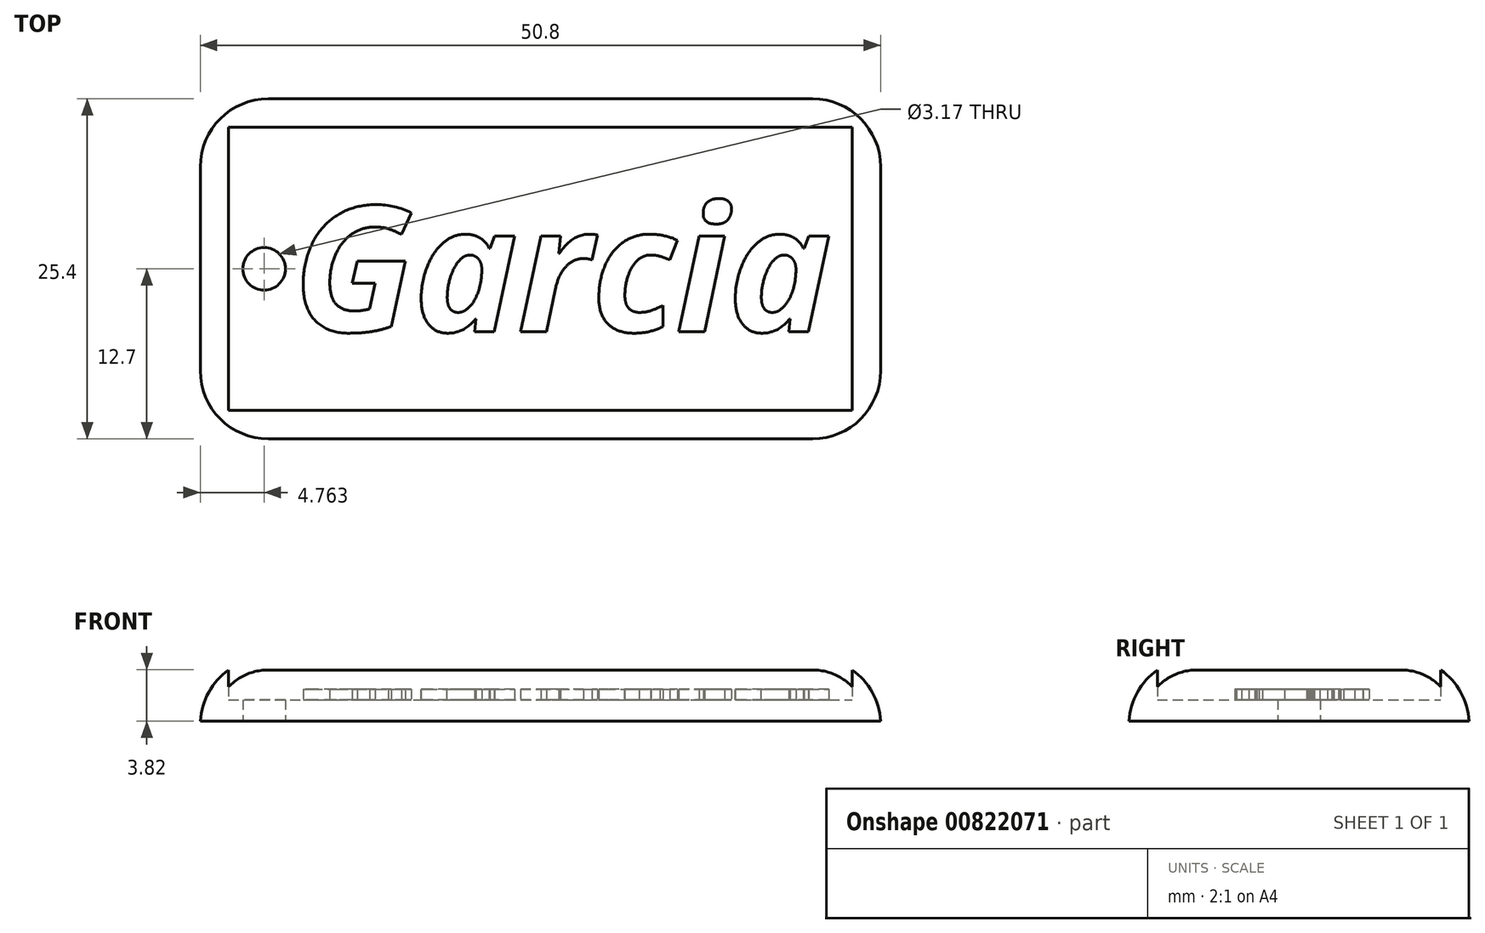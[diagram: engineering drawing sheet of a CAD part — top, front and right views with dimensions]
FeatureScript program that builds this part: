
annotation { "Feature Type Name" : "Feature", "Feature Type Description" : "" }
export const myFeature = defineFeature(function(context is Context, id is Id, definition is map)
    precondition{}
    {
        {
            var Q0;
            Q0=qCreatedBy(makeId("Top.planeOp"),FACE);
            var sketch = newSketch(context, id + "F0", { "sketchPlane" : qUnion([Q0])});
            skLineSegment(sketch, "E0.bottom", {"start": v(0, 0) * mm, "end": v(50.8, 0) * mm});
            skLineSegment(sketch, "E0.top", {"start": v(0, 25.4) * mm, "end": v(50.8, 25.4) * mm});
            skLineSegment(sketch, "E0.left", {"start": v(0, 0) * mm, "end": v(0, 25.4) * mm});
            skLineSegment(sketch, "E0.right", {"start": v(50.8, 0) * mm, "end": v(50.8, 25.4) * mm});
            skCircle(sketch, "E1", {"center": v(4.76, 12.7) * mm, "radius": 1.59 * mm});
            skPoint(sketch, "E1.centerSnap0", {"position": v(0, 12.7) * mm});
            skLineSegment(sketch, "E2.0", {"start": v(2.12, 23.28) * mm, "end": v(48.68, 23.28) * mm});
            skLineSegment(sketch, "E2.1", {"start": v(2.12, 2.12) * mm, "end": v(2.12, 23.28) * mm});
            skLineSegment(sketch, "E2.2", {"start": v(2.12, 2.12) * mm, "end": v(48.68, 2.12) * mm});
            skLineSegment(sketch, "E2.3", {"start": v(48.68, 2.12) * mm, "end": v(48.68, 23.28) * mm});
            skSolve(sketch);
        }
        {
            var Q0;
            Q0=makeQuery(id+"F0.imprint","IMPRINT",FACE,{"disambiguationData":[TD([[makeQuery(id+"F0.imprint","IMPRINT",EDGE,{"derivedFrom":sQuery(id+"F0.wireOp",EDGE,"E1")}),-1.0]])]});
            extrude(context, id + "F1", {"entities" : qUnion([Q0]), "depth" : 1.59 * mm, "offsetDistance" : 25.4 * mm});
        }
        {
            var Q0;
            Q0 = qSketchRegion(id + "F0", true);
            extrude(context, id + "F2", {"entities" : qUnion([Q0]), "operationType" : NewBodyOperationType.ADD, "depth" : 4.76 * mm, "offsetDistance" : 25.4 * mm});
        }
        {
            var Q0;
            Q0=makeQuery(id+"F2.opExtrude","SWEPT_EDGE",EDGE,{"disambiguationData":[OSD([sQuery(id+"F0.wireOp",EDGE,"E0.bottom"),sQuery(id+"F0.wireOp",EDGE,"E0.right")])]});
            var Q1;
            Q1=makeQuery(id+"F2.opExtrude","SWEPT_EDGE",EDGE,{"disambiguationData":[OSD([sQuery(id+"F0.wireOp",EDGE,"E0.top"),sQuery(id+"F0.wireOp",EDGE,"E0.right")])]});
            var Q2;
            Q2=makeQuery(id+"F2.opExtrude","SWEPT_EDGE",EDGE,{"disambiguationData":[OSD([sQuery(id+"F0.wireOp",EDGE,"E0.top"),sQuery(id+"F0.wireOp",EDGE,"E0.left")])]});
            var Q3;
            Q3=makeQuery(id+"F2.opExtrude","SWEPT_EDGE",EDGE,{"disambiguationData":[OSD([sQuery(id+"F0.wireOp",EDGE,"E0.bottom"),sQuery(id+"F0.wireOp",EDGE,"E0.left")])]});
            fillet(context, id + "F3", {"entities" : qUnion([Q0, Q1, Q2, Q3]), "radius" : 5.08 * mm, "tangentPropagation" : true, "allowEdgeOverflow" : false});
        }
        {
            var Q0;
            Q0=makeQuery(id+"F1.opExtrude","CAP_FACE",FACE,{"disambiguationData":[OSD([sQuery(id+"F0.wireOp",EDGE,"E1"),sQuery(id+"F0.wireOp",EDGE,"E2.0"),sQuery(id+"F0.wireOp",EDGE,"E2.1"),sQuery(id+"F0.wireOp",EDGE,"E2.2"),sQuery(id+"F0.wireOp",EDGE,"E2.3")])],"isStart":false});
            var sketch = newSketch(context, id + "F4", { "sketchPlane" : qUnion([Q0])});
            skText(sketch, "E3", { "text": "Garcia", "fontName": "OpenSans-BoldItalic.ttf"});
            const initialGuessF4  = {"E3": [0.0069, 0.00802, 1, 0, 0.00941]};
            skSetInitialGuess(sketch, initialGuessF4);
            skSolve(sketch);
        }
        {
            var Q0;
            Q0 = qSketchRegion(id + "F4", true);
            extrude(context, id + "F5", {"entities" : qUnion([Q0]), "operationType" : NewBodyOperationType.ADD, "depth" : 0.8 * mm, "offsetDistance" : 25.4 * mm});
        }
        {
            var Q0;
            Q0=makeQuery(id+"F2.opExtrude","CAP_EDGE",EDGE,{"disambiguationData":[OSD([sQuery(id+"F0.wireOp",EDGE,"E0.bottom")])],"isStart":false});
            var Q1;
            Q1=makeQuery(id+"F2.opExtrude","CAP_EDGE",EDGE,{"disambiguationData":[OSD([sQuery(id+"F0.wireOp",EDGE,"E0.top")])],"isStart":false});
            var Q2;
            Q2=makeQuery(id+"F2.opExtrude","CAP_EDGE",EDGE,{"disambiguationData":[OSD([sQuery(id+"F0.wireOp",EDGE,"E0.right")])],"isStart":false});
            var Q3;
            Q3=makeQuery(id+"F2.opExtrude","CAP_EDGE",EDGE,{"disambiguationData":[OSD([sQuery(id+"F0.wireOp",EDGE,"E0.left")])],"isStart":false});
            fillet(context, id + "F6", {"entities" : qUnion([Q0, Q1, Q2, Q3]), "radius" : 5.08 * mm, "tangentPropagation" : true, "allowEdgeOverflow" : false});
        }
    });
